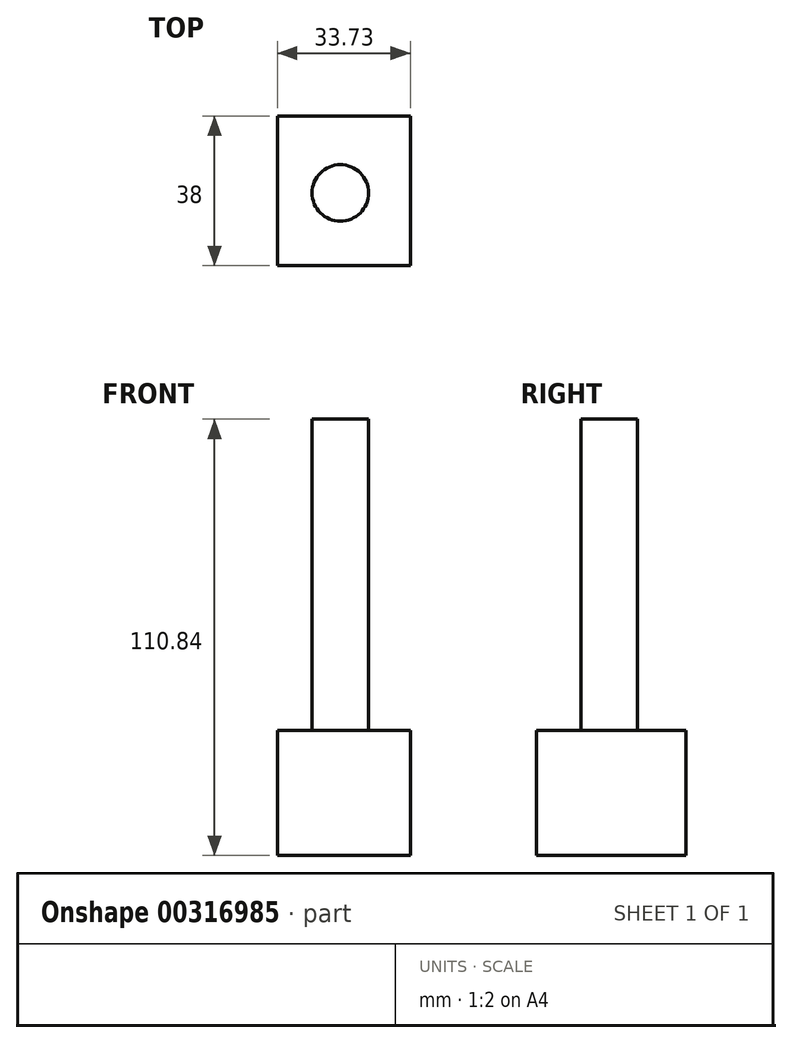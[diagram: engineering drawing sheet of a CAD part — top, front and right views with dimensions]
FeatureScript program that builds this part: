
annotation { "Feature Type Name" : "Feature", "Feature Type Description" : "" }
export const myFeature = defineFeature(function(context is Context, id is Id, definition is map)
    precondition{}
    {
        {
            var Q0;
            Q0=qCreatedBy(makeId("Front.planeOp"),FACE);
            var sketch = newSketch(context, id + "F0", { "sketchPlane" : qUnion([Q0])});
            skLineSegment(sketch, "E0.bottom", {"start": v(-33.73, 31.74) * mm, "end": v(0, 31.74) * mm});
            skLineSegment(sketch, "E0.top", {"start": v(-33.73, 0) * mm, "end": v(0, 0) * mm});
            skLineSegment(sketch, "E0.left", {"start": v(-33.73, 31.74) * mm, "end": v(-33.73, 0) * mm});
            skLineSegment(sketch, "E0.right", {"start": v(0, 31.74) * mm, "end": v(0, 0) * mm});
            skSolve(sketch);
        }
        {
            var Q0;
            Q0=makeQuery(id+"F0.imprint","IMPRINT",FACE,{"disambiguationData":[TD([[makeQuery(id+"F0.imprint","IMPRINT",EDGE,{"derivedFrom":sQuery(id+"F0.wireOp",EDGE,"E0.bottom")}),-1.0]])]});
            extrude(context, id + "F1", {"entities" : qUnion([Q0]), "depth" : 38 * mm});
        }
        {
            var Q0;
            Q0=makeQuery(id+"F1.opExtrude","SWEPT_FACE",FACE,{"disambiguationData":[OSD([sQuery(id+"F0.wireOp",EDGE,"E0.bottom")])]});
            var sketch = newSketch(context, id + "F2", { "sketchPlane" : qUnion([Q0])});
            skCircle(sketch, "E1", {"center": v(-17.8, -19.52) * mm, "radius": 7.18 * mm});
            skSolve(sketch);
        }
        {
            var Q0;
            Q0=makeQuery(id+"F2.imprint","IMPRINT",FACE,{"disambiguationData":[TD([[makeQuery(id+"F2.imprint","IMPRINT",EDGE,{"derivedFrom":sQuery(id+"F2.wireOp",EDGE,"E1")}),1.0]])]});
            extrude(context, id + "F3", {"entities" : qUnion([Q0]), "operationType" : NewBodyOperationType.ADD, "depth" : 79.1 * mm});
        }
    });
